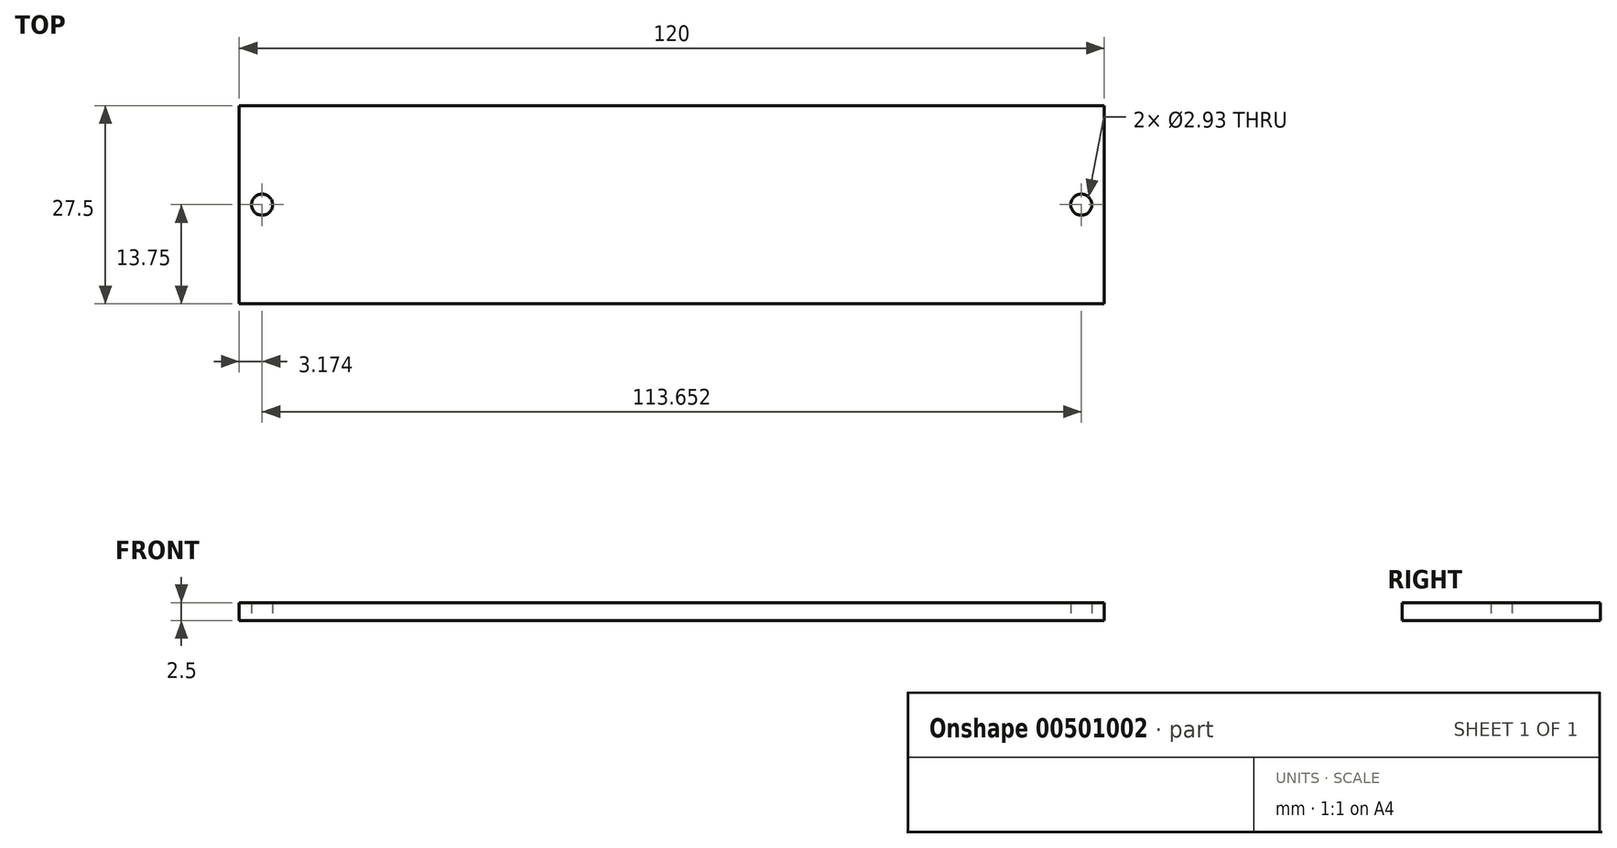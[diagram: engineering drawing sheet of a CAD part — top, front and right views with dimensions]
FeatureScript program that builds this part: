
annotation { "Feature Type Name" : "Feature", "Feature Type Description" : "" }
export const myFeature = defineFeature(function(context is Context, id is Id, definition is map)
    precondition{}
    {
        {
            var Q0;
            Q0=qCreatedBy(makeId("Top.planeOp"),FACE);
            var sketch = newSketch(context, id + "F0", { "sketchPlane" : qUnion([Q0])});
            skLineSegment(sketch, "E0.bottom", {"start": v(60, 13.75) * mm, "end": v(-60, 13.75) * mm});
            skLineSegment(sketch, "E0.top", {"start": v(60, -13.75) * mm, "end": v(-60, -13.75) * mm});
            skLineSegment(sketch, "E0.left", {"start": v(60, 13.75) * mm, "end": v(60, -13.75) * mm});
            skLineSegment(sketch, "E0.right", {"start": v(-60, 13.75) * mm, "end": v(-60, -13.75) * mm});
            skPoint(sketch, "E0.middle", {"position": v(0, 0) * mm});
            skCircle(sketch, "E1", {"center": v(-56.83, 0) * mm, "radius": 1.47 * mm});
            skCircle(sketch, "E2.MirrorC", {"center": v(56.83, 0) * mm, "radius": 1.47 * mm});
            skSolve(sketch);
        }
        {
            var Q0;
            Q0=makeQuery(id+"F0.imprint","IMPRINT",FACE,{"disambiguationData":[TD([[makeQuery(id+"F0.imprint","IMPRINT",EDGE,{"derivedFrom":sQuery(id+"F0.wireOp",EDGE,"E0.bottom")}),1.0]])]});
            extrude(context, id + "F1", {"entities" : qUnion([Q0]), "depth" : 2.5 * mm, "offsetDistance" : 25 * mm});
        }
    });
